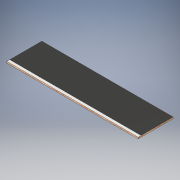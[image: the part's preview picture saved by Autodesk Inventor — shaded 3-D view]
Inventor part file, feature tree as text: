
AUTODESK INVENTOR PART (.ipt)
format: ipt  version: 2017 (Build 210142000, 142)  size: 103,936 bytes
history: native  units: in
note: dims shown in document units (in); Inventor stores cm internally (conversion verified against a paired STEP export)
features: extrude x2, sketch x2
ambient origin geometry x8: Origin, YZ Plane, XZ Plane, XY Plane, X Axis, Y Axis, Z Axis, Center Point
bodies: Solid1 (feature_tree)
feature tree (4):
  extrude  "Extrusion1"  Depth=12.0in
  extrude  "Extrusion2"  Depth=1.0in
  sketch  "Sketch1"  dims[d0=45.0in d1=12.0in]
  sketch  "Sketch2"  dims[d2=0.5in d3=0.0in d4=1.0in d5=0.001in d6=0.0in]
